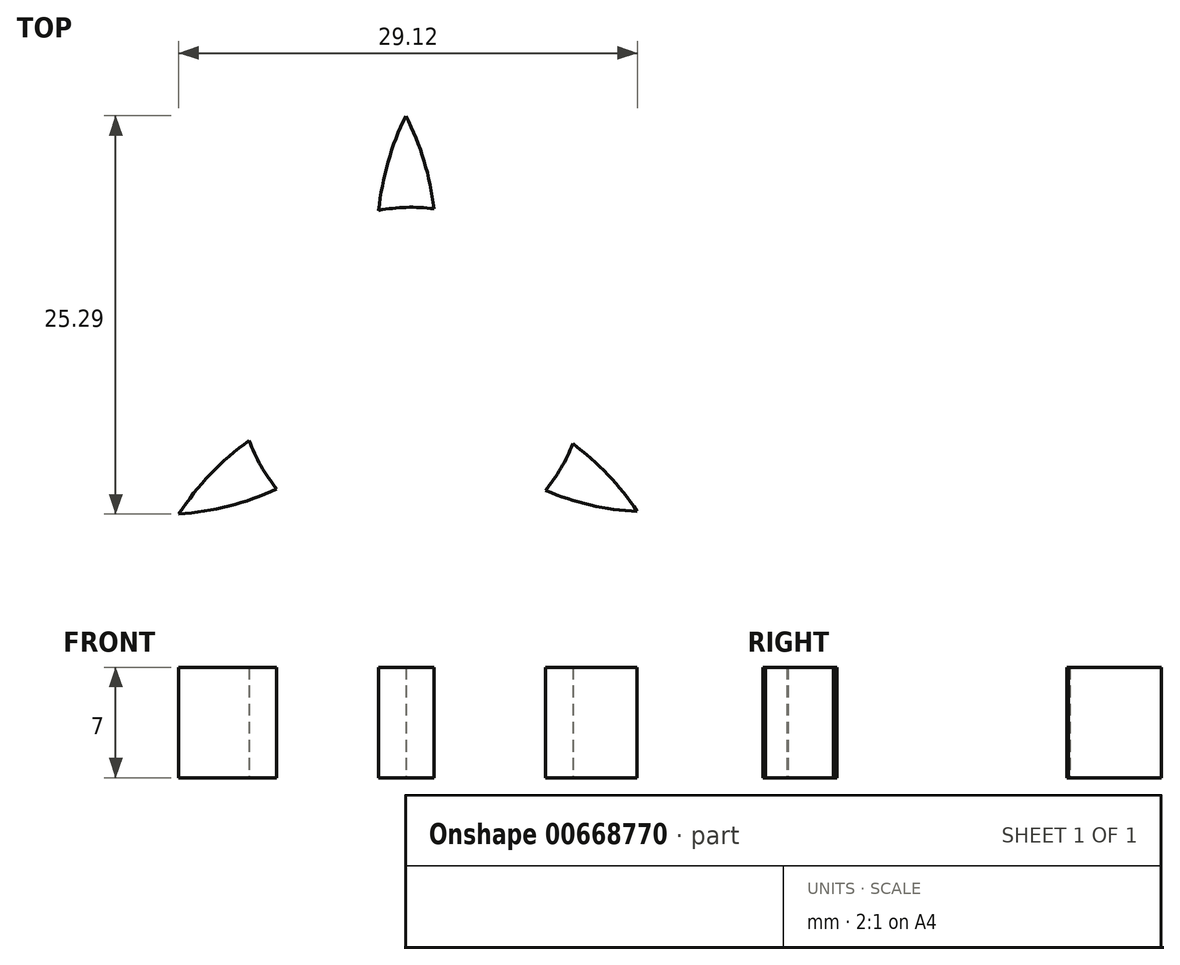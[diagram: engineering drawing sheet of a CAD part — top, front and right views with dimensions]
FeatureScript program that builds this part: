
annotation { "Feature Type Name" : "Feature", "Feature Type Description" : "" }
export const myFeature = defineFeature(function(context is Context, id is Id, definition is map)
    precondition{}
    {
        {
            var Q0;
            Q0=qCreatedBy(makeId("Top.planeOp"),FACE);
            var sketch = newSketch(context, id + "F0", { "sketchPlane" : qUnion([Q0])});
            skCircle(sketch, "E0", {"center": v(0, 0) * mm, "radius": 11 * mm});
            skCircle(sketch, "E1", {"center": v(0, 27.07) * mm, "radius": 3.17 * mm});
            skArc(sketch, "E2", {"start": v(7.02, 24.44) * mm, "mid": v(-0.39, 34.56) * mm, "end": v(-6.71, 23.72) * mm});
            skArc(sketch, "E3.1.0", {"start": v(-25.09, -5.9) * mm, "mid": v(-30.15, -17.38) * mm, "end": v(-17.6, -17.44) * mm});
            skCircle(sketch, "E3.1.1", {"center": v(-23.85, -13.3) * mm, "radius": 3.17 * mm});
            skArc(sketch, "E3.2.0", {"start": v(17.24, -18.54) * mm, "mid": v(29.71, -17.18) * mm, "end": v(23.49, -6.29) * mm});
            skCircle(sketch, "E3.2.1", {"center": v(23.03, -13.77) * mm, "radius": 3.17 * mm});
            skPoint(sketch, "E3.center", {"position": v(-0.28, 0) * mm});
            skArc(sketch, "E4", {"start": v(7.02, 24.44) * mm, "mid": v(-1.13, 15.02) * mm, "end": v(-0.91, 2.57) * mm});
            skArc(sketch, "E5.1.0", {"start": v(-25.09, -5.9) * mm, "mid": v(-12.86, -8.25) * mm, "end": v(-2.18, -1.84) * mm});
            skArc(sketch, "E5.2.0", {"start": v(17.24, -18.54) * mm, "mid": v(13.16, -6.77) * mm, "end": v(2.27, -0.73) * mm});
            skArc(sketch, "E6", {"start": v(-0.91, 2.57) * mm, "mid": v(3.24, 2) * mm, "end": v(6.72, 4.35) * mm});
            skArc(sketch, "E7", {"start": v(2.56, -2.87) * mm, "mid": v(5.66, 0.16) * mm, "end": v(6.72, 4.35) * mm});
            skArc(sketch, "E8.1.0", {"start": v(-2.18, -1.84) * mm, "mid": v(-3.77, 2.04) * mm, "end": v(-7.54, 3.88) * mm});
            skArc(sketch, "E8.1.1", {"start": v(0.8, 3.9) * mm, "mid": v(-3.38, 5.06) * mm, "end": v(-7.54, 3.88) * mm});
            skArc(sketch, "E8.2.0", {"start": v(2.27, -0.73) * mm, "mid": v(-0.3, -4.05) * mm, "end": v(0, -8.23) * mm});
            skArc(sketch, "E8.2.1", {"start": v(-4.18, -1.02) * mm, "mid": v(-3.1, -5.21) * mm, "end": v(0, -8.23) * mm});
            skArc(sketch, "E9.trimOffspring", {"start": v(2.56, -2.87) * mm, "mid": v(12.45, -8.13) * mm, "end": v(23.49, -6.29) * mm});
            skArc(sketch, "E10.trimOffspring", {"start": v(0.8, 3.9) * mm, "mid": v(0.4, 15.08) * mm, "end": v(-6.71, 23.72) * mm});
            skArc(sketch, "E11.trimOffspring", {"start": v(-4.18, -1.02) * mm, "mid": v(-13.67, -6.95) * mm, "end": v(-17.6, -17.44) * mm});
            skCircle(sketch, "E12.cCircle", {"center": v(0, 27.07) * mm, "radius": 3.17 * mm, "construction": true});
            skLineSegment(sketch, "E12.0", {"start": v(3.18, 27.07) * mm, "end": v(1.59, 24.32) * mm});
            skLineSegment(sketch, "E12.1", {"start": v(1.59, 24.32) * mm, "end": v(-1.59, 24.32) * mm});
            skLineSegment(sketch, "E12.2", {"start": v(-1.59, 24.32) * mm, "end": v(-3.18, 27.07) * mm});
            skLineSegment(sketch, "E12.3", {"start": v(-3.18, 27.07) * mm, "end": v(-1.59, 29.82) * mm});
            skLineSegment(sketch, "E12.4", {"start": v(-1.59, 29.82) * mm, "end": v(1.59, 29.82) * mm});
            skLineSegment(sketch, "E12.5", {"start": v(1.59, 29.82) * mm, "end": v(3.17, 27.07) * mm});
            skSolve(sketch);
        }
        {
            var Q0;
            Q0=makeQuery(id+"F0.imprint","IMPRINT",FACE,{"disambiguationData":[TD([[makeQuery(id+"F0.imprint","IMPRINT",EDGE,{"derivedFrom":sQuery(id+"F0.wireOp",EDGE,"E0")}),-1.0]])]});
            extrude(context, id + "F1", {"entities" : qUnion([Q0]), "depth" : 7 * mm, "offsetDistance" : 25 * mm});
        }
    });
